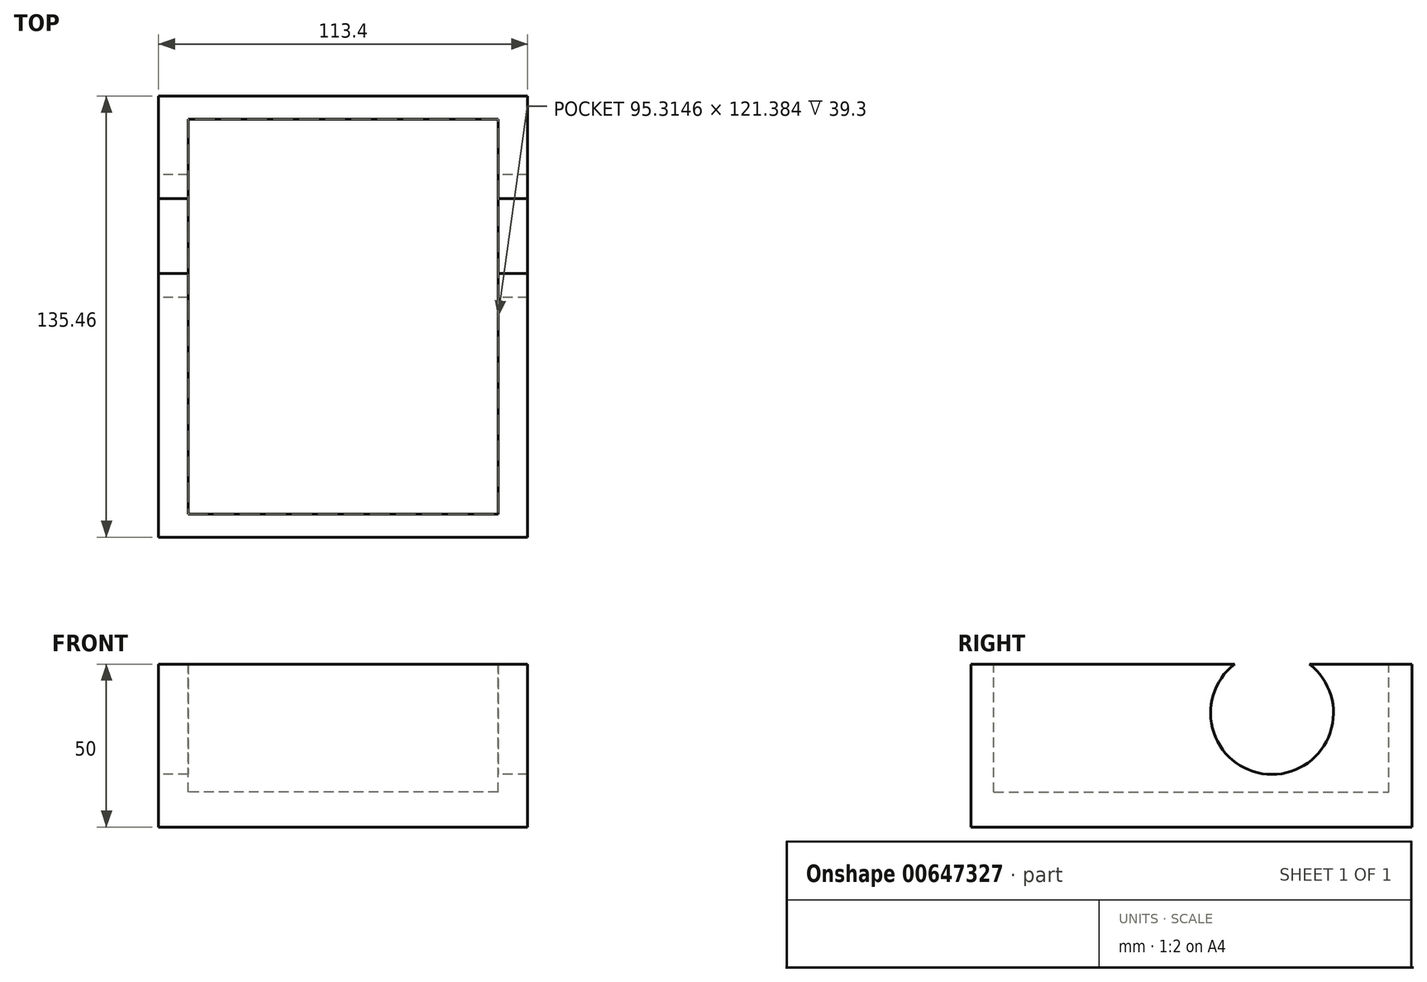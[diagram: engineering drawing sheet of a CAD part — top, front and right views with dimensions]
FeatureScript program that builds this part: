
annotation { "Feature Type Name" : "Feature", "Feature Type Description" : "" }
export const myFeature = defineFeature(function(context is Context, id is Id, definition is map)
    precondition{}
    {
        {
            var Q0;
            Q0=qCreatedBy(makeId("Top.planeOp"),FACE);
            var sketch = newSketch(context, id + "F0", { "sketchPlane" : qUnion([Q0])});
            skLineSegment(sketch, "E0.bottom", {"start": v(-56.7, -67.73) * mm, "end": v(56.7, -67.73) * mm});
            skLineSegment(sketch, "E0.top", {"start": v(-56.7, 67.73) * mm, "end": v(56.7, 67.73) * mm});
            skLineSegment(sketch, "E0.left", {"start": v(-56.7, -67.73) * mm, "end": v(-56.7, 67.73) * mm});
            skLineSegment(sketch, "E0.right", {"start": v(56.7, -67.73) * mm, "end": v(56.7, 67.73) * mm});
            skPoint(sketch, "E0.middle", {"position": v(0, 0) * mm});
            skSolve(sketch);
        }
        {
            var Q0;
            Q0=makeQuery(id+"F0.imprint","IMPRINT",FACE,{"disambiguationData":[TD([[makeQuery(id+"F0.imprint","IMPRINT",EDGE,{"derivedFrom":sQuery(id+"F0.wireOp",EDGE,"E0.bottom")}),1.0]])]});
            extrude(context, id + "F1", {"entities" : qUnion([Q0]), "depth" : 50 * mm, "offsetDistance" : 25 * mm});
        }
        {
            var Q0;
            Q0=makeQuery(id+"F1.opExtrude","CAP_FACE",FACE,{"disambiguationData":[OSD([sQuery(id+"F0.wireOp",EDGE,"E0.bottom"),sQuery(id+"F0.wireOp",EDGE,"E0.top"),sQuery(id+"F0.wireOp",EDGE,"E0.left"),sQuery(id+"F0.wireOp",EDGE,"E0.right")])],"isStart":false});
            var sketch = newSketch(context, id + "F2", { "sketchPlane" : qUnion([Q0])});
            skLineSegment(sketch, "E1.bottom", {"start": v(47.66, -60.7) * mm, "end": v(-47.66, -60.7) * mm});
            skLineSegment(sketch, "E1.top", {"start": v(47.66, 60.7) * mm, "end": v(-47.66, 60.7) * mm});
            skLineSegment(sketch, "E1.left", {"start": v(47.66, -60.7) * mm, "end": v(47.66, 60.7) * mm});
            skLineSegment(sketch, "E1.right", {"start": v(-47.66, -60.7) * mm, "end": v(-47.66, 60.7) * mm});
            skPoint(sketch, "E1.middle", {"position": v(0, 0) * mm});
            skSolve(sketch);
        }
        {
            var Q0;
            Q0=makeQuery(id+"F2.imprint","IMPRINT",FACE,{"disambiguationData":[TD([[makeQuery(id+"F2.imprint","IMPRINT",EDGE,{"derivedFrom":sQuery(id+"F2.wireOp",EDGE,"E1.bottom")}),-1.0]])]});
            extrude(context, id + "F3", {"entities" : qUnion([Q0]), "operationType" : NewBodyOperationType.REMOVE, "oppositeDirection" : true, "depth" : 39.3 * mm, "offsetDistance" : 25 * mm});
        }
        {
            var Q0;
            Q0=makeQuery(id+"F1.opExtrude","SWEPT_FACE",FACE,{"disambiguationData":[OSD([sQuery(id+"F0.wireOp",EDGE,"E0.left")])]});
            var sketch = newSketch(context, id + "F4", { "sketchPlane" : qUnion([Q0])});
            skCircle(sketch, "E2", {"center": v(-24.77, 35.04) * mm, "radius": 18.89 * mm});
            skSolve(sketch);
        }
        {
            var Q0;
            Q0=makeQuery(id+"F4.imprint","IMPRINT",FACE,{"disambiguationData":[TD([[makeQuery(id+"F4.imprint","IMPRINT",EDGE,{"derivedFrom":sQuery(id+"F4.wireOp",EDGE,"E2")}),1.0]])]});
            extrude(context, id + "F5", {"entities" : qUnion([Q0]), "operationType" : NewBodyOperationType.REMOVE, "oppositeDirection" : true, "depth" : 200 * mm, "offsetDistance" : 25 * mm});
        }
    });
